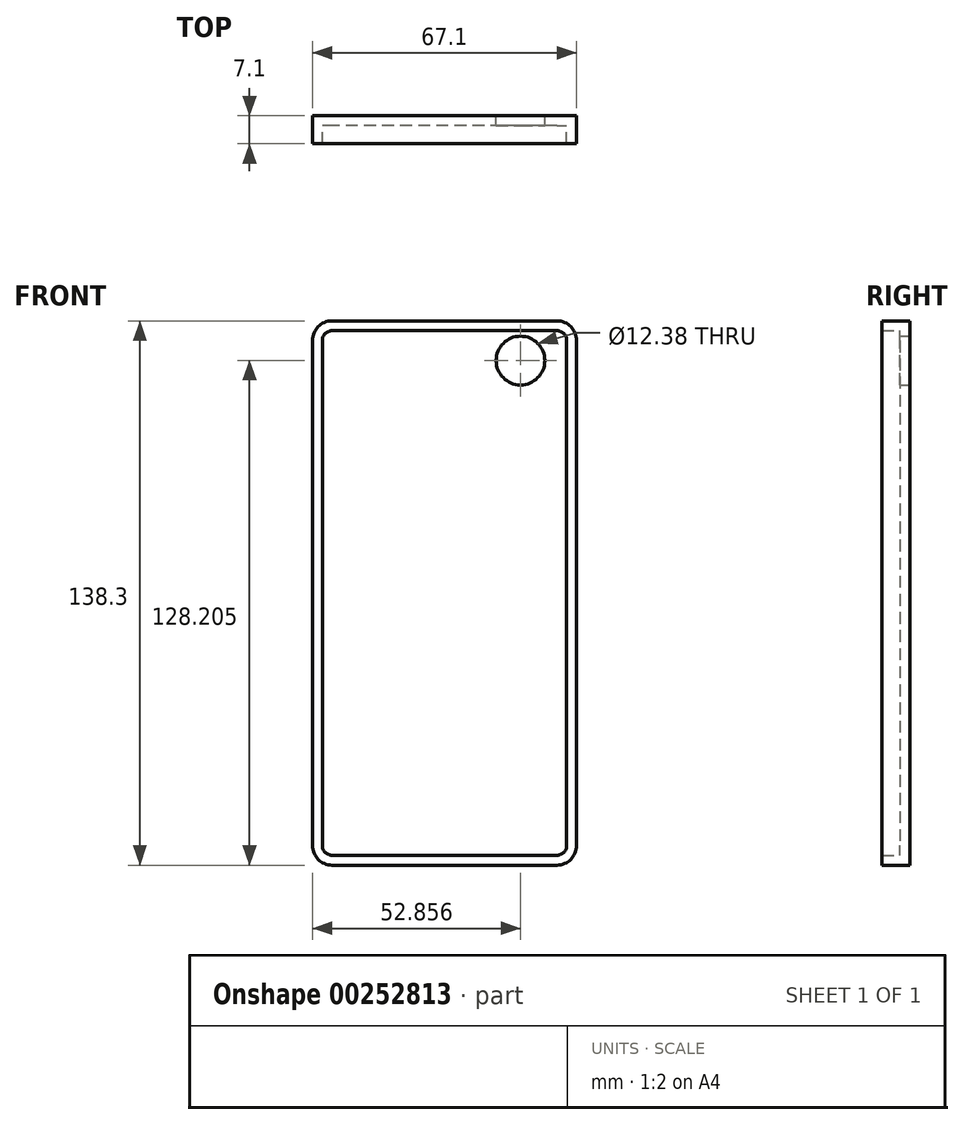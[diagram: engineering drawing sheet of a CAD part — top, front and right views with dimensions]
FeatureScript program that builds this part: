
annotation { "Feature Type Name" : "Feature", "Feature Type Description" : "" }
export const myFeature = defineFeature(function(context is Context, id is Id, definition is map)
    precondition{}
    {
        {
            var Q0;
            Q0=qCreatedBy(makeId("Front.planeOp"),FACE);
            var sketch = newSketch(context, id + "F0", { "sketchPlane" : qUnion([Q0])});
            skLineSegment(sketch, "E0.bottom", {"start": v(33.55, 69.15) * mm, "end": v(-33.55, 69.15) * mm});
            skLineSegment(sketch, "E0.top", {"start": v(33.55, -69.15) * mm, "end": v(-33.55, -69.15) * mm});
            skLineSegment(sketch, "E0.left", {"start": v(33.55, 69.15) * mm, "end": v(33.55, -69.15) * mm});
            skLineSegment(sketch, "E0.right", {"start": v(-33.55, 69.15) * mm, "end": v(-33.55, -69.15) * mm});
            skPoint(sketch, "E0.middle", {"position": v(0, 0) * mm});
            skSolve(sketch);
        }
        {
            var Q0;
            Q0=makeQuery(id+"F0.imprint","IMPRINT",FACE,{"disambiguationData":[TD([[makeQuery(id+"F0.imprint","IMPRINT",EDGE,{"derivedFrom":sQuery(id+"F0.wireOp",EDGE,"E0.bottom")}),1.0]])]});
            extrude(context, id + "F1", {"entities" : qUnion([Q0]), "depth" : 7.1 * mm, "symmetric" : true});
        }
        {
            var Q0;
            Q0=makeQuery(id+"F1.opExtrude","SWEPT_EDGE",EDGE,{"disambiguationData":[OSD([sQuery(id+"F0.wireOp",EDGE,"E0.bottom"),sQuery(id+"F0.wireOp",EDGE,"E0.right")])]});
            var Q1;
            Q1=makeQuery(id+"F1.opExtrude","SWEPT_EDGE",EDGE,{"disambiguationData":[OSD([sQuery(id+"F0.wireOp",EDGE,"E0.bottom"),sQuery(id+"F0.wireOp",EDGE,"E0.left")])]});
            var Q2;
            Q2=makeQuery(id+"F1.opExtrude","SWEPT_EDGE",EDGE,{"disambiguationData":[OSD([sQuery(id+"F0.wireOp",EDGE,"E0.top"),sQuery(id+"F0.wireOp",EDGE,"E0.left")])]});
            var Q3;
            Q3=makeQuery(id+"F1.opExtrude","SWEPT_EDGE",EDGE,{"disambiguationData":[OSD([sQuery(id+"F0.wireOp",EDGE,"E0.top"),sQuery(id+"F0.wireOp",EDGE,"E0.right")])]});
            fillet(context, id + "F2", {"entities" : qUnion([Q0, Q1, Q2, Q3]), "radius" : 5 * mm, "tangentPropagation" : true, "allowEdgeOverflow" : false});
        }
        {
            var Q0;
            Q0=makeQuery(id+"F1.opExtrude","CAP_FACE",FACE,{"disambiguationData":[OSD([sQuery(id+"F0.wireOp",EDGE,"E0.bottom"),sQuery(id+"F0.wireOp",EDGE,"E0.top"),sQuery(id+"F0.wireOp",EDGE,"E0.left"),sQuery(id+"F0.wireOp",EDGE,"E0.right")])],"isStart":false});
            shell(context, id + "F3", {"entities" : qUnion([Q0]), "thickness" : 2.5 * mm});
        }
        {
            var Q0;
            Q0=qCreatedBy(makeId("Front.planeOp"),FACE);
            var sketch = newSketch(context, id + "F4", { "sketchPlane" : qUnion([Q0])});
            skCircle(sketch, "E1", {"center": v(19.3, 59.05) * mm, "radius": 6.2 * mm});
            skSolve(sketch);
        }
        {
            var Q0;
            Q0=makeQuery(id+"F4.imprint","IMPRINT",FACE,{"disambiguationData":[TD([[makeQuery(id+"F4.imprint","IMPRINT",EDGE,{"derivedFrom":sQuery(id+"F4.wireOp",EDGE,"E1")}),1.0]])]});
            extrude(context, id + "F5", {"entities" : qUnion([Q0]), "operationType" : NewBodyOperationType.REMOVE, "depth" : 25 * mm, "symmetric" : true});
        }
    });
